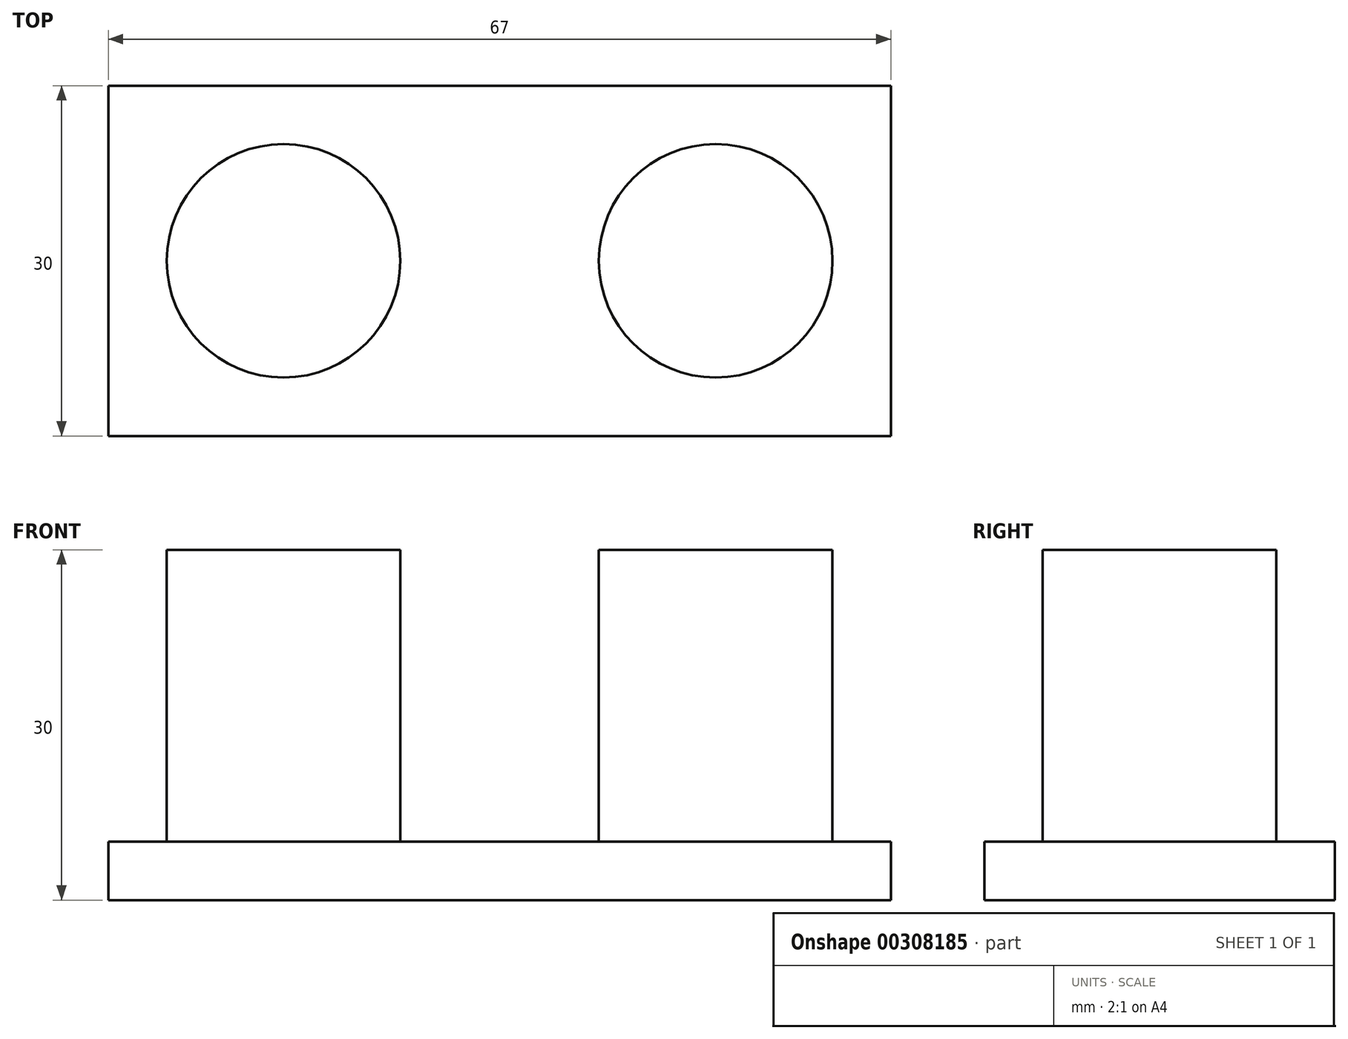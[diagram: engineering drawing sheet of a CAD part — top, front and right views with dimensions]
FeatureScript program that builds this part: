
annotation { "Feature Type Name" : "Feature", "Feature Type Description" : "" }
export const myFeature = defineFeature(function(context is Context, id is Id, definition is map)
    precondition{}
    {
        {
            var Q0;
            Q0=qCreatedBy(makeId("Top.planeOp"),FACE);
            var sketch = newSketch(context, id + "F0", { "sketchPlane" : qUnion([Q0])});
            skCircle(sketch, "E0", {"center": v(0, 0) * mm, "radius": 10 * mm});
            skLineSegment(sketch, "E1", {"start": v(0, 0) * mm, "end": v(37, 0) * mm});
            skCircle(sketch, "E2", {"center": v(37, 0) * mm, "radius": 10 * mm});
            skLineSegment(sketch, "E3", {"start": v(0, 0) * mm, "end": v(-15, 0) * mm});
            skLineSegment(sketch, "E4", {"start": v(-15, 0) * mm, "end": v(-15, -15) * mm});
            skLineSegment(sketch, "E5", {"start": v(-15, -15) * mm, "end": v(52, -15) * mm});
            skLineSegment(sketch, "E6", {"start": v(52, -15) * mm, "end": v(52, 0) * mm});
            skLineSegment(sketch, "E7", {"start": v(52, 0) * mm, "end": v(37, 0) * mm});
            skLineSegment(sketch, "E8", {"start": v(52, 15) * mm, "end": v(52, 0) * mm});
            skLineSegment(sketch, "E9", {"start": v(-15, 0) * mm, "end": v(-15, 15) * mm});
            skLineSegment(sketch, "E10", {"start": v(-15, 15) * mm, "end": v(52, 15) * mm});
            skSolve(sketch);
        }
        {
            var Q0;
            {var subQ0=sQuery(id+"F0.wireOp",EDGE,"E4");Q0=makeQuery(id+"F0.imprint","IMPRINT",FACE,{"disambiguationData":[TD([[makeQuery(id+"F0.imprint","IMPRINT",EDGE,{"derivedFrom":subQ0}),1.0]])]});}
            var sketch = newSketch(context, id + "F1", { "sketchPlane" : qUnion([Q0])});
            skSolve(sketch);
        }
        {
            var Q0;
            Q0 = qSketchRegion(id + "F1", true);
            var Q1;
            {var subQ8=sQuery(id+"F0.wireOp",EDGE,"E8");Q1=makeQuery(id+"F0.imprint","IMPRINT",FACE,{"disambiguationData":[TD([[makeQuery(id+"F0.imprint","IMPRINT",EDGE,{"derivedFrom":subQ8}),-1.0]])]});}
            var Q2;
            {var subQ0=sQuery(id+"F0.wireOp",EDGE,"E4");Q2=makeQuery(id+"F0.imprint","IMPRINT",FACE,{"disambiguationData":[TD([[makeQuery(id+"F0.imprint","IMPRINT",EDGE,{"derivedFrom":subQ0}),1.0]])]});}
            extrude(context, id + "F2", {"entities" : qUnion([Q0, Q1, Q2]), "depth" : 5 * mm});
        }
        {
            var Q0;
            {var subQ0=sQuery(id+"F0.wireOp",EDGE,"E1");var subQ1=sQuery(id+"F0.wireOp",EDGE,"E0");var subQ2=makeQuery(id+"F0.imprint","INTERSECT",VERTEX,{"derivedFrom":[subQ1,subQ0]});Q0=makeQuery(id+"F0.imprint","IMPRINT",FACE,{"disambiguationData":[TD([[makeQuery(id+"F0.imprint","IMPRINT",EDGE,{"disambiguationData":[TD([[subQ2,-1.0]])],"derivedFrom":subQ1}),1.0]])]});}
            var Q1;
            {var subQ0=sQuery(id+"F0.wireOp",EDGE,"E1");var subQ1=sQuery(id+"F0.wireOp",EDGE,"E0");var subQ2=makeQuery(id+"F0.imprint","INTERSECT",VERTEX,{"derivedFrom":[subQ1,subQ0]});Q1=makeQuery(id+"F0.imprint","IMPRINT",FACE,{"disambiguationData":[TD([[makeQuery(id+"F0.imprint","IMPRINT",EDGE,{"disambiguationData":[TD([[subQ2,1.0]])],"derivedFrom":subQ1}),1.0]])]});}
            var Q2;
            {var subQ0=sQuery(id+"F0.wireOp",EDGE,"E7");var subQ1=sQuery(id+"F0.wireOp",EDGE,"E1");var subQ2=makeQuery(id+"F0.imprint","INTERSECT",VERTEX,{"derivedFrom":[subQ1,subQ0]});Q2=makeQuery(id+"F0.imprint","IMPRINT",FACE,{"disambiguationData":[TD([[makeQuery(id+"F0.imprint","IMPRINT",EDGE,{"disambiguationData":[TD([[subQ2,1.0]])],"derivedFrom":subQ1}),-1.0]])]});}
            var Q3;
            {var subQ0=sQuery(id+"F0.wireOp",EDGE,"E7");var subQ1=sQuery(id+"F0.wireOp",EDGE,"E1");var subQ2=makeQuery(id+"F0.imprint","INTERSECT",VERTEX,{"derivedFrom":[subQ1,subQ0]});Q3=makeQuery(id+"F0.imprint","IMPRINT",FACE,{"disambiguationData":[TD([[makeQuery(id+"F0.imprint","IMPRINT",EDGE,{"disambiguationData":[TD([[subQ2,1.0]])],"derivedFrom":subQ1}),1.0]])]});}
            extrude(context, id + "F3", {"entities" : qUnion([Q0, Q1, Q2, Q3]), "operationType" : NewBodyOperationType.ADD, "depth" : 30 * mm});
        }
    });
